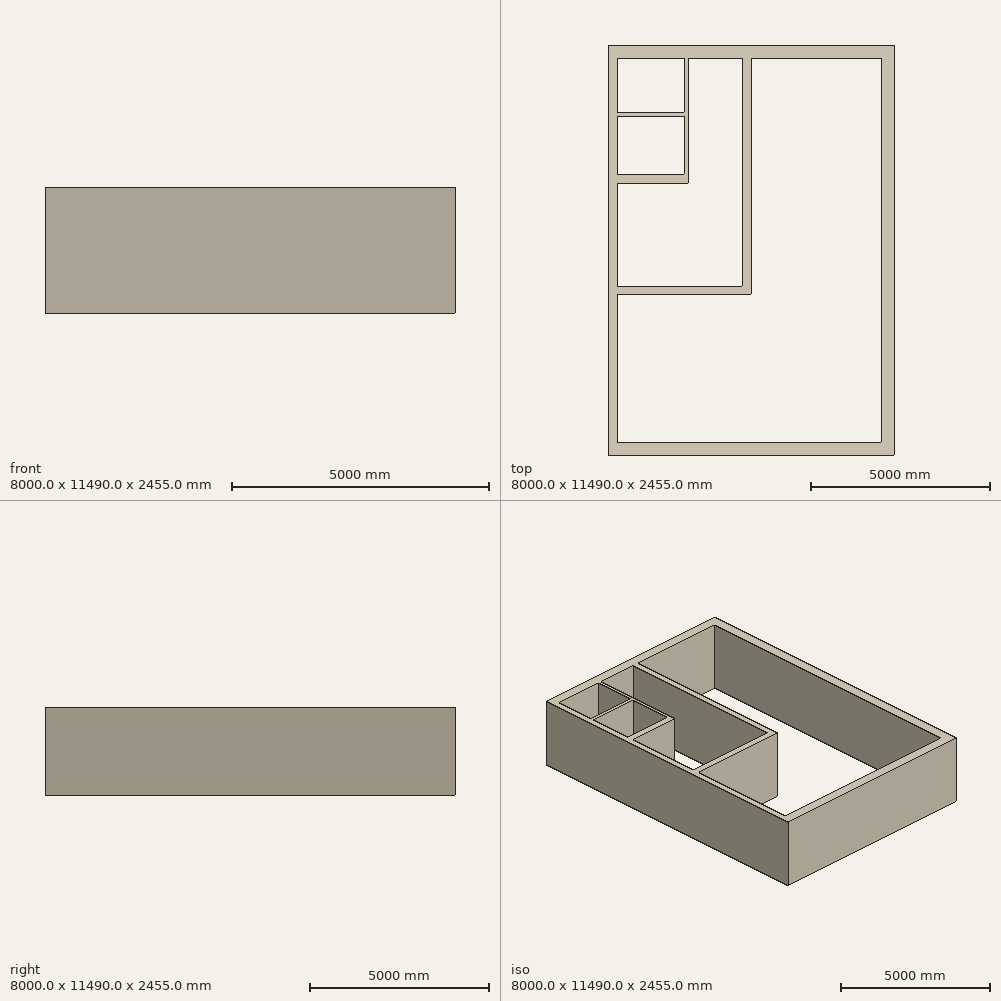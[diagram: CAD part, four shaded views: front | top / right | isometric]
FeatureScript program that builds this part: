
annotation { "Feature Type Name" : "Feature", "Feature Type Description" : "" }
export const myFeature = defineFeature(function(context is Context, id is Id, definition is map)
    precondition{}
    {
        {
            var Q0;
            Q0=qCreatedBy(makeId("Top.planeOp"),FACE);
            var sketch = newSketch(context, id + "F0", { "sketchPlane" : qUnion([Q0])});
            skLineSegment(sketch, "E0.bottom", {"start": v(0, 0) * mm, "end": v(8000, 0) * mm});
            skLineSegment(sketch, "E0.top", {"start": v(0, 11490) * mm, "end": v(8000, 11490) * mm});
            skLineSegment(sketch, "E0.left", {"start": v(0, 0) * mm, "end": v(0, 11490) * mm});
            skLineSegment(sketch, "E0.right", {"start": v(8000, 0) * mm, "end": v(8000, 11490) * mm});
            skLineSegment(sketch, "E1.bottom", {"start": v(240, 11125) * mm, "end": v(7635, 11125) * mm});
            skLineSegment(sketch, "E1.top", {"start": v(240, 365) * mm, "end": v(7635, 365) * mm});
            skLineSegment(sketch, "E1.left", {"start": v(240, 11125) * mm, "end": v(240, 365) * mm});
            skLineSegment(sketch, "E1.right", {"start": v(7635, 11125) * mm, "end": v(7635, 365) * mm});
            skSolve(sketch);
        }
        {
            var Q0;
            Q0=makeQuery(id+"F0.imprint","IMPRINT",FACE,{"disambiguationData":[TD([[makeQuery(id+"F0.imprint","IMPRINT",EDGE,{"derivedFrom":sQuery(id+"F0.wireOp",EDGE,"E0.bottom")}),1.0]])]});
            extrude(context, id + "F1", {"entities" : qUnion([Q0]), "depth" : 2455 * mm});
        }
        {
            var Q0;
            Q0=qCreatedBy(makeId("Top.planeOp"),FACE);
            var sketch = newSketch(context, id + "F2", { "sketchPlane" : qUnion([Q0])});
            skLineSegment(sketch, "E2.bottom", {"start": v(240, 11125) * mm, "end": v(3990, 11125) * mm});
            skLineSegment(sketch, "E2.top", {"start": v(240, 4500) * mm, "end": v(3990, 4500) * mm});
            skLineSegment(sketch, "E2.left", {"start": v(240, 11125) * mm, "end": v(240, 4500) * mm});
            skLineSegment(sketch, "E2.right", {"start": v(3990, 11125) * mm, "end": v(3990, 4500) * mm});
            skLineSegment(sketch, "E3.0", {"start": v(240, 4740) * mm, "end": v(3750, 4740) * mm});
            skLineSegment(sketch, "E3.3", {"start": v(3750, 11125) * mm, "end": v(3750, 4740) * mm});
            skSolve(sketch);
        }
        {
            var Q0;
            {var subQ2=sQuery(id+"F2.wireOp",EDGE,"E2.top");Q0=makeQuery(id+"F2.imprint","IMPRINT",FACE,{"disambiguationData":[TD([[makeQuery(id+"F2.imprint","IMPRINT",EDGE,{"derivedFrom":subQ2}),1.0]])]});}
            var Q1;
            Q1=makeQuery(id+"F1.opExtrude","CAP_FACE",FACE,{"disambiguationData":[OSD([sQuery(id+"F0.wireOp",EDGE,"E0.bottom"),sQuery(id+"F0.wireOp",EDGE,"E0.top"),sQuery(id+"F0.wireOp",EDGE,"E0.left"),sQuery(id+"F0.wireOp",EDGE,"E0.right"),sQuery(id+"F0.wireOp",EDGE,"E1.bottom"),sQuery(id+"F0.wireOp",EDGE,"E1.top"),sQuery(id+"F0.wireOp",EDGE,"E1.left"),sQuery(id+"F0.wireOp",EDGE,"E1.right")])],"isStart":false});
            extrude(context, id + "F3", {"entities" : qUnion([Q0]), "operationType" : NewBodyOperationType.ADD, "endBound" : BoundingType.UP_TO_SURFACE, "endBoundEntityFace" : qUnion([Q1]), "depth" : 25 * mm});
        }
        {
            var Q0;
            Q0=qCreatedBy(makeId("Top.planeOp"),FACE);
            var sketch = newSketch(context, id + "F4", { "sketchPlane" : qUnion([Q0])});
            skLineSegment(sketch, "E4.top", {"start": v(240, 9615) * mm, "end": v(2125, 9615) * mm});
            skLineSegment(sketch, "E4.right", {"start": v(2125, 11125) * mm, "end": v(2125, 9615) * mm});
            skLineSegment(sketch, "E5.bottom", {"start": v(240, 9500) * mm, "end": v(2125, 9500) * mm});
            skLineSegment(sketch, "E5.top", {"start": v(240, 7865) * mm, "end": v(2125, 7865) * mm});
            skLineSegment(sketch, "E5.right", {"start": v(2125, 9500) * mm, "end": v(2125, 7865) * mm});
            skLineSegment(sketch, "E6", {"start": v(2125, 11125) * mm, "end": v(2240, 11125) * mm});
            skLineSegment(sketch, "E7", {"start": v(2240, 11125) * mm, "end": v(2240, 7625) * mm});
            skLineSegment(sketch, "E8", {"start": v(2240, 7625) * mm, "end": v(240, 7625) * mm});
            skLineSegment(sketch, "E9", {"start": v(240, 7625) * mm, "end": v(240, 7865) * mm});
            skLineSegment(sketch, "E10", {"start": v(240, 9500) * mm, "end": v(240, 9615) * mm});
            skSolve(sketch);
        }
        {
            var Q0;
            Q0=makeQuery(id+"F4.imprint","IMPRINT",FACE,{"disambiguationData":[TD([[makeQuery(id+"F4.imprint","IMPRINT",EDGE,{"derivedFrom":sQuery(id+"F4.wireOp",EDGE,"E4.top")}),-1.0]])]});
            var Q1;
            {var subQ0=sQuery(id+"F0.wireOp",EDGE,"E1.right");var subQ1=sQuery(id+"F0.wireOp",EDGE,"E1.left");var subQ2=sQuery(id+"F0.wireOp",EDGE,"E1.top");var subQ3=sQuery(id+"F0.wireOp",EDGE,"E1.bottom");var subQ4=sQuery(id+"F0.wireOp",EDGE,"E0.right");var subQ5=sQuery(id+"F0.wireOp",EDGE,"E0.left");var subQ6=sQuery(id+"F0.wireOp",EDGE,"E0.top");var subQ7=sQuery(id+"F0.wireOp",EDGE,"E0.bottom");Q1=makeQuery(id+"F3.boolean.opBoolean","MERGE",FACE,{"derivedFrom":[makeQuery(id+"F1.opExtrude","CAP_FACE",FACE,{"disambiguationData":[OSD([subQ7,subQ6,subQ5,subQ4,subQ3,subQ2,subQ1,subQ0])],"isStart":false}),makeQuery(id+"F3.opExtrude","CAP_FACE",FACE,{"disambiguationData":[OSD([subQ7,subQ6,subQ5,subQ4,subQ3,subQ2,subQ1,subQ0])],"isStart":false})]});}
            extrude(context, id + "F5", {"entities" : qUnion([Q0]), "operationType" : NewBodyOperationType.ADD, "endBound" : BoundingType.UP_TO_SURFACE, "endBoundEntityFace" : qUnion([Q1]), "depth" : 25 * mm});
        }
    });
